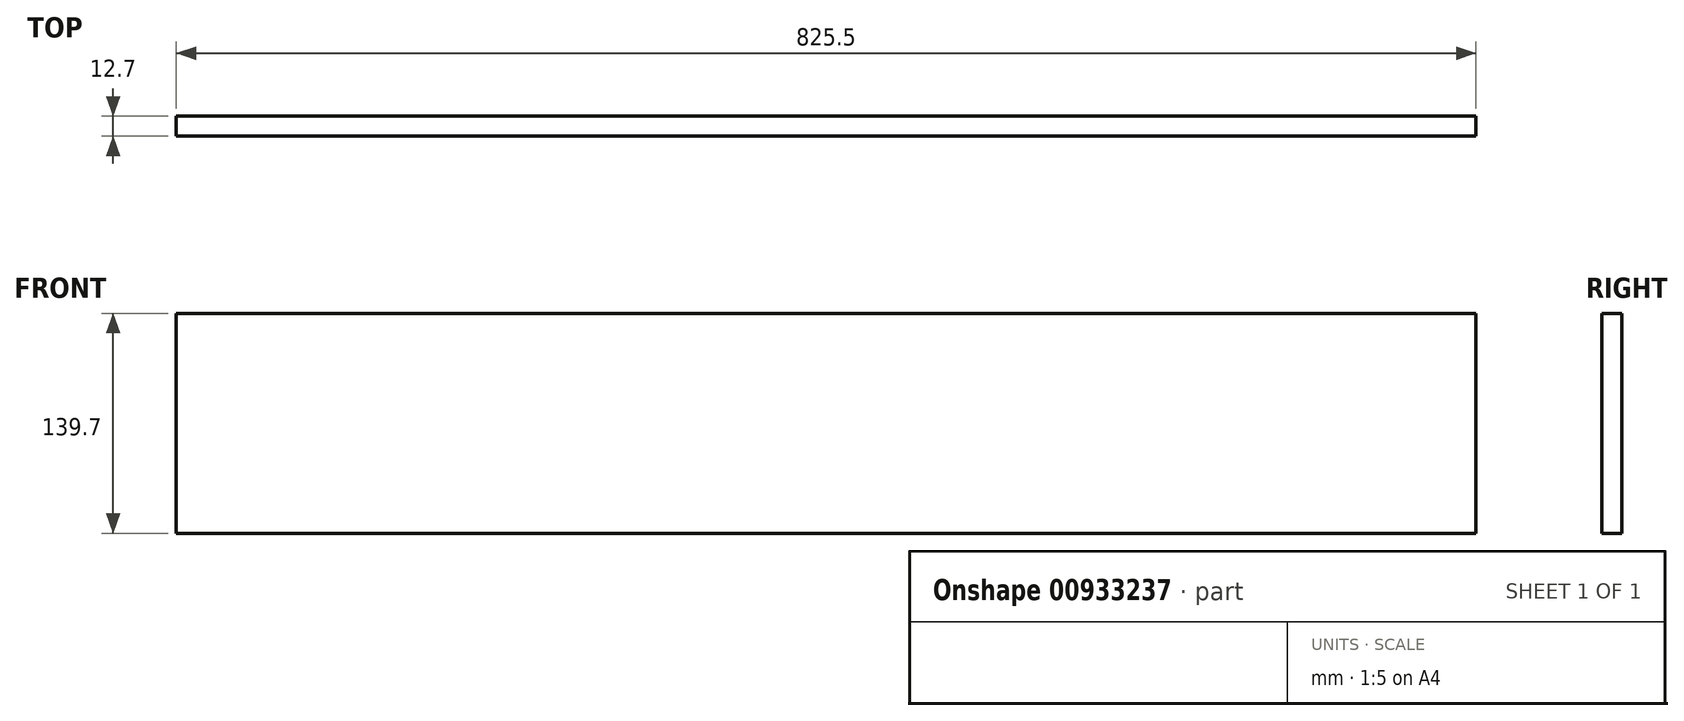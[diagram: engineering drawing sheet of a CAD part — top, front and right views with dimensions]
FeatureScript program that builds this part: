
annotation { "Feature Type Name" : "Feature", "Feature Type Description" : "" }
export const myFeature = defineFeature(function(context is Context, id is Id, definition is map)
    precondition{}
    {
        {
            var Q0;
            Q0=qCreatedBy(makeId("Front.planeOp"),FACE);
            var sketch = newSketch(context, id + "F0", { "sketchPlane" : qUnion([Q0])});
            skLineSegment(sketch, "E0.bottom", {"start": v(412.75, 69.85) * mm, "end": v(-412.75, 69.85) * mm});
            skLineSegment(sketch, "E0.top", {"start": v(412.75, -69.85) * mm, "end": v(-412.75, -69.85) * mm});
            skLineSegment(sketch, "E0.left", {"start": v(412.75, 69.85) * mm, "end": v(412.75, -69.85) * mm});
            skLineSegment(sketch, "E0.right", {"start": v(-412.75, 69.85) * mm, "end": v(-412.75, -69.85) * mm});
            skPoint(sketch, "E0.middle", {"position": v(0, 0) * mm});
            skSolve(sketch);
        }
        {
            var Q0;
            Q0=qSketchRegion(id+"F0",true);
            extrude(context, id + "F1", {"entities" : qUnion([Q0]), "depth" : 12.7 * mm, "offsetDistance" : 25.4 * mm});
        }
    });
